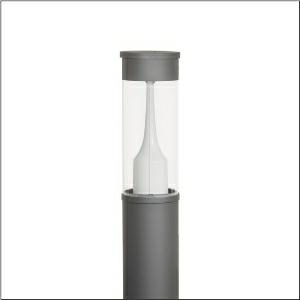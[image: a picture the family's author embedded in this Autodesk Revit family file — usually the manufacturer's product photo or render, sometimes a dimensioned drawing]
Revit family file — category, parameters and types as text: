
# Revit family: city-light_260_iq___st1_2a_5xa5295ef14h_2f06
name_source: partatom
category: Lighting Fixtures
units: mm (PartAtom-declared; Revit-internal decimal feet)

## family parameters
Cut with Voids When Loaded = No
Host = Face
Light Source = No
Part Type = Normal
Room Calculation Point = No
Round Connector Dimension = Use Diameter
Shared = No

## types (1)
- --- (1 x LED, 1540 lm, 10.5 W, 3000K)
    Apparent Load = 11 VA
    CIE Flux Codes = 22 61 93 96 100
    Color Rendering = 70
    Color Temperature = 3000K
    Default Elevation = 1800 mm
    Description = City-Light 260 iQ, light pillar, Module 540 iQ-SR, primary light control with 3 zone facetted reflector, of plastic, silver coated, highly specular, structured, primary optical cover: cover, of PMMA, transparent, light distribution: ST1.2a, primary light characteristic: asymmetric, LED, High Power LED, rated luminous flux: 1.540lm, luminous efficacy: 147lm/W, light colour: 730, colour temperature: 3000K, control gear: iQ Street-Remote, control: Auto-Match, Temp-Guard, Lumen-Switch, Night-Set, Smart-Wire, Light-Fading, Desk-Remote (wireless, voltage-free reading and setting of iQ features in the workshop via application-optimized NFC function/RFID function), optimised constant luminous flux control (CLO 2.0), Street-Remote, pre-setting: logarithmic dimming characteristic, with terminal, 6-pole, max. 2.5mm², mains connection: 230..240V, AC, 50/60Hz, start of lifetime: 11W, end of service life: 11W, reduction: 5W, luminaire housing, cylindrical, of extruded aluminium section, coated, Siteco® metallic grey (DB 702S), length: 2.600mm, diameter: 200mm, Module 540 iQ-SR, traffic white (RAL 9016), equipment: standard, protection rating (complete): IP65, insulation class (complete): insulation class II (safety insulation), certification: CE, ENEC, VDE, packaging unit: 1 piece

Light Distribution: ST1.2a
    Height = 500 mm
    Lamp = 1 x LED
    Lamp Light Flux = 1540 lm
    Lamp Power = 10.5 W
    Lamp count = 1
    Length = 200 mm
    Luminous efficacy = 147 lm/W
    Manufacturer = Siteco
    ModVariant = No
    Model = 5XA5295EF14H
    Mounting Place = Floor
    Mounting Type = Freestanding
    Number of Poles = 1
    OnlyDefault = Yes
    Power Factor = 1
    Product Name = City-Light 260 iQ | ST1.2a
    Product group = light pillar
    ProductGroupID = 1301
    Protection Class = Protection class II
    Protection Degree = IP 65
    RLX_Detail_Level = 1
    RLX_Emergency_Light_Flux = 0 lm
    RLX_Emergency_Type = 0
    RLX_Emergency_Type_DB = No
    RlxData = <blob elided: 60589 chars, md5=a1ea3d6d>
    Socket = socket
    Standby Power = 0 W
    System Light Flux = 1540 lm
    System Power = 11 W
    Type Comments = factory setting: luminous flux: 100 % | dim-lin: 254 | 419 mA
    Type Image = l_1006918.jpg
    URL = http://relux.com
    VarID = @adj_158681
    Voltage = 0 V
    Weight = 0.00 kg
    Width = 0 mm  [stored 0 ft]

note: [stored X ft] marks values corroborated as IEEE doubles in the binary element streams (Revit-internal decimal feet)

## geometry (parser evidence)
native form markers: Blend x4, Sweep x11
no freeform markers — native parametric forms only
